# Revit family: ElectricalFixture_WiringAccessories_Hager_Sollyster_Telephone&Data
name_source: partatom
category: Electrical Fixtures
revit_build: Autodesk Revit 2015 (Build: 20160512_1515(x64)
units: mm (PartAtom-declared; Revit-internal decimal feet)

## types (4) — shared parameters
CE Approval = Yes
Colour = SollystaWhite
Default Elevation = 1219.2 mm  [stored 4 ft]
Design Country = China
Expected Life = 25 years
Extrusion From Wall = 11.9 mm
Finish = Gloss
Flex Outlet = No
Frequency = 50/60Hz
Gross Weight kg = 0.165
LED Indicator Switch = No
Manufacturer = Hager
Manufacturer Country = United Kingdom
Manufacturer Website = http://www.hager.co.uk
Material = Urea Formaldehyde Thermoset Plastic
Overall Depth = 26.1 mm
Overall Height = 86 mm  [stored 0.282152 ft]
Overall Length = 86 mm  [stored 0.282152 ft]
Overall Width = 86 mm  [stored 0.282152 ft]
Packaging Recyclable = Yes
Product Family = WhiteMouldedTelephone_TV&Data
Product Group = WiringAccessories
Product Literature = http://www.hager.co.uk
Product Range = Sollysta
Product URL = http://www.hager.co.uk
Reference Standard = BS 1363-2
Shape = Rectangular
Shipping Weight kg = 0.188
Supply Phase = 1
Switch = Yes
Type = ElectricalFixture
Voltage (Volts) = 230V/240V

## per-type parameters (varying)
| type | Description | EAN Code | Features | Name | Technical Description |
| WMBTM | BTMasterTelephoneOutlet | 5015652261629 | BTMasterTelephoneOutlet | WhiteMouldedTelephone_TV&Data_WMBTM | BTMasterTelephoneOutlet |
| WMBTS | BTSecondaryTelephoneOutlet | 5015652261636 | BTSecondaryTelephoneOutlet | WhiteMouldedTelephone_TV&Data_WMBTS | BTSecondaryTelephoneOutlet |
| WMRJ11 | RJ11Socket | 5015652261650 | RJ11Socket | WhiteMouldedTelephone_TV&Data_WMRJ11 | RJ11Socket |
| WMRJ45 | RJ45Socket | 5015652261643 | RJ45Socket | WhiteMouldedTelephone_TV&Data_WMRJ45 | RJ45Socket |

note: column(s) folded — value = type name in every type: Product Model Number, Unique Reference

note: [stored X ft] marks values corroborated as IEEE doubles in the binary element streams (Revit-internal decimal feet)

## geometry (parser evidence)
native form markers: Blend x4, Sweep x3
no freeform markers — native parametric forms only
